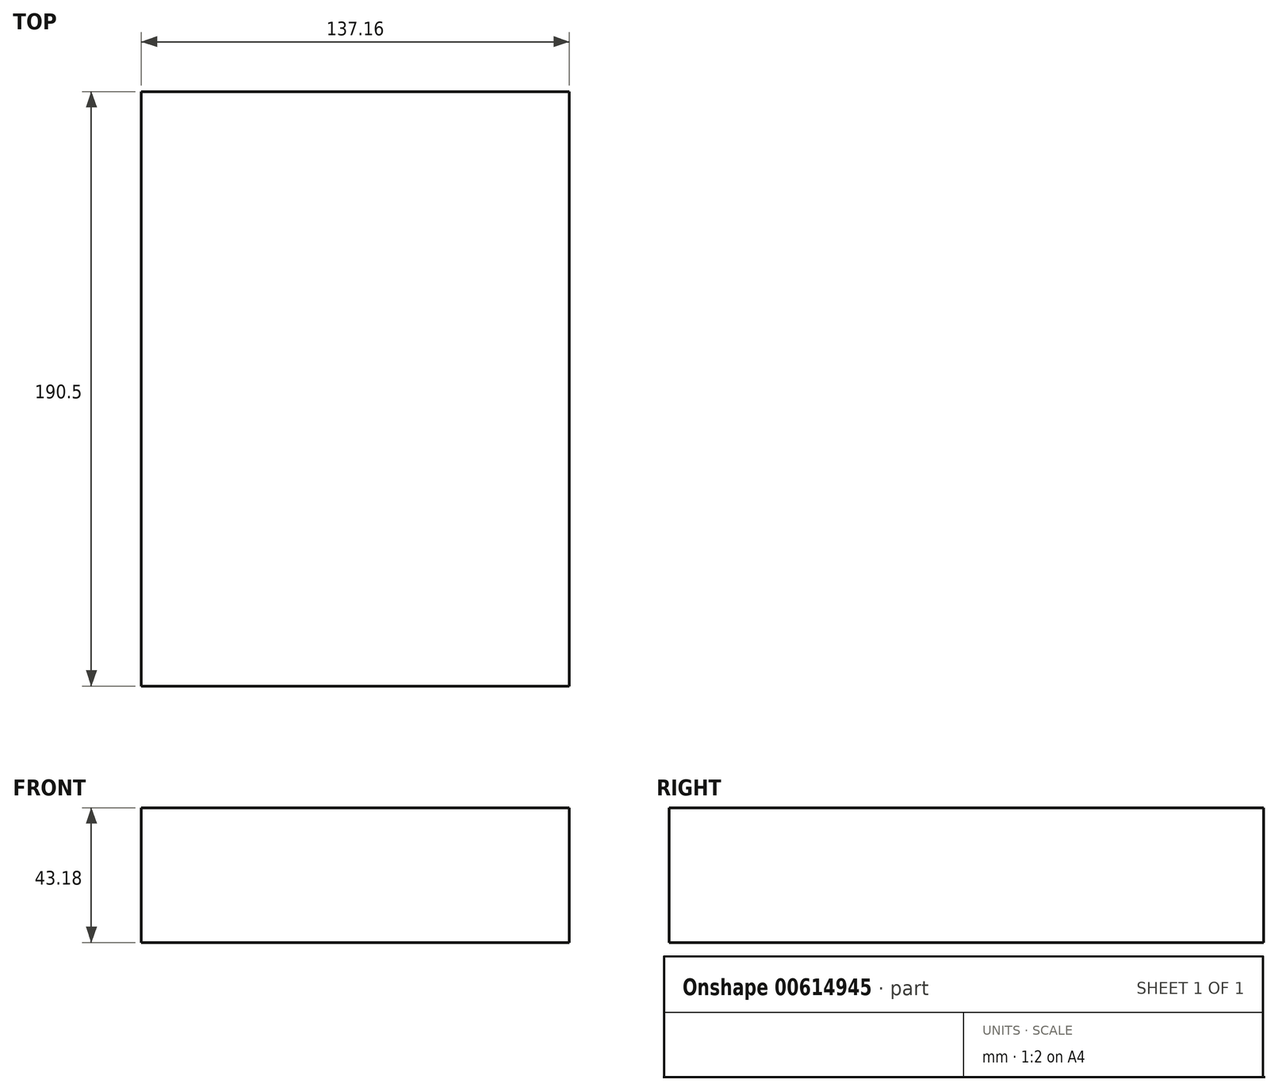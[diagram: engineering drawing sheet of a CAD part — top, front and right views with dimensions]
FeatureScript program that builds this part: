
annotation { "Feature Type Name" : "Feature", "Feature Type Description" : "" }
export const myFeature = defineFeature(function(context is Context, id is Id, definition is map)
    precondition{}
    {
        {
            var Q0;
            Q0=qCreatedBy(makeId("Top.planeOp"),FACE);
            var sketch = newSketch(context, id + "F0", { "sketchPlane" : qUnion([Q0])});
            skLineSegment(sketch, "E0.bottom", {"start": v(68.58, 95.25) * mm, "end": v(-68.58, 95.25) * mm});
            skLineSegment(sketch, "E0.top", {"start": v(68.58, -95.25) * mm, "end": v(-68.58, -95.25) * mm});
            skLineSegment(sketch, "E0.left", {"start": v(68.58, 95.25) * mm, "end": v(68.58, -95.25) * mm});
            skLineSegment(sketch, "E0.right", {"start": v(-68.58, 95.25) * mm, "end": v(-68.58, -95.25) * mm});
            skPoint(sketch, "E0.middle", {"position": v(0, 0) * mm});
            skSolve(sketch);
        }
        {
            var Q0;
            Q0=makeQuery(id+"F0.imprint","IMPRINT",FACE,{"disambiguationData":[TD([[makeQuery(id+"F0.imprint","IMPRINT",EDGE,{"derivedFrom":sQuery(id+"F0.wireOp",EDGE,"E0.bottom")}),1.0]])]});
            extrude(context, id + "F1", {"entities" : qUnion([Q0]), "depth" : 43.18 * mm, "offsetDistance" : 25 * mm});
        }
    });
